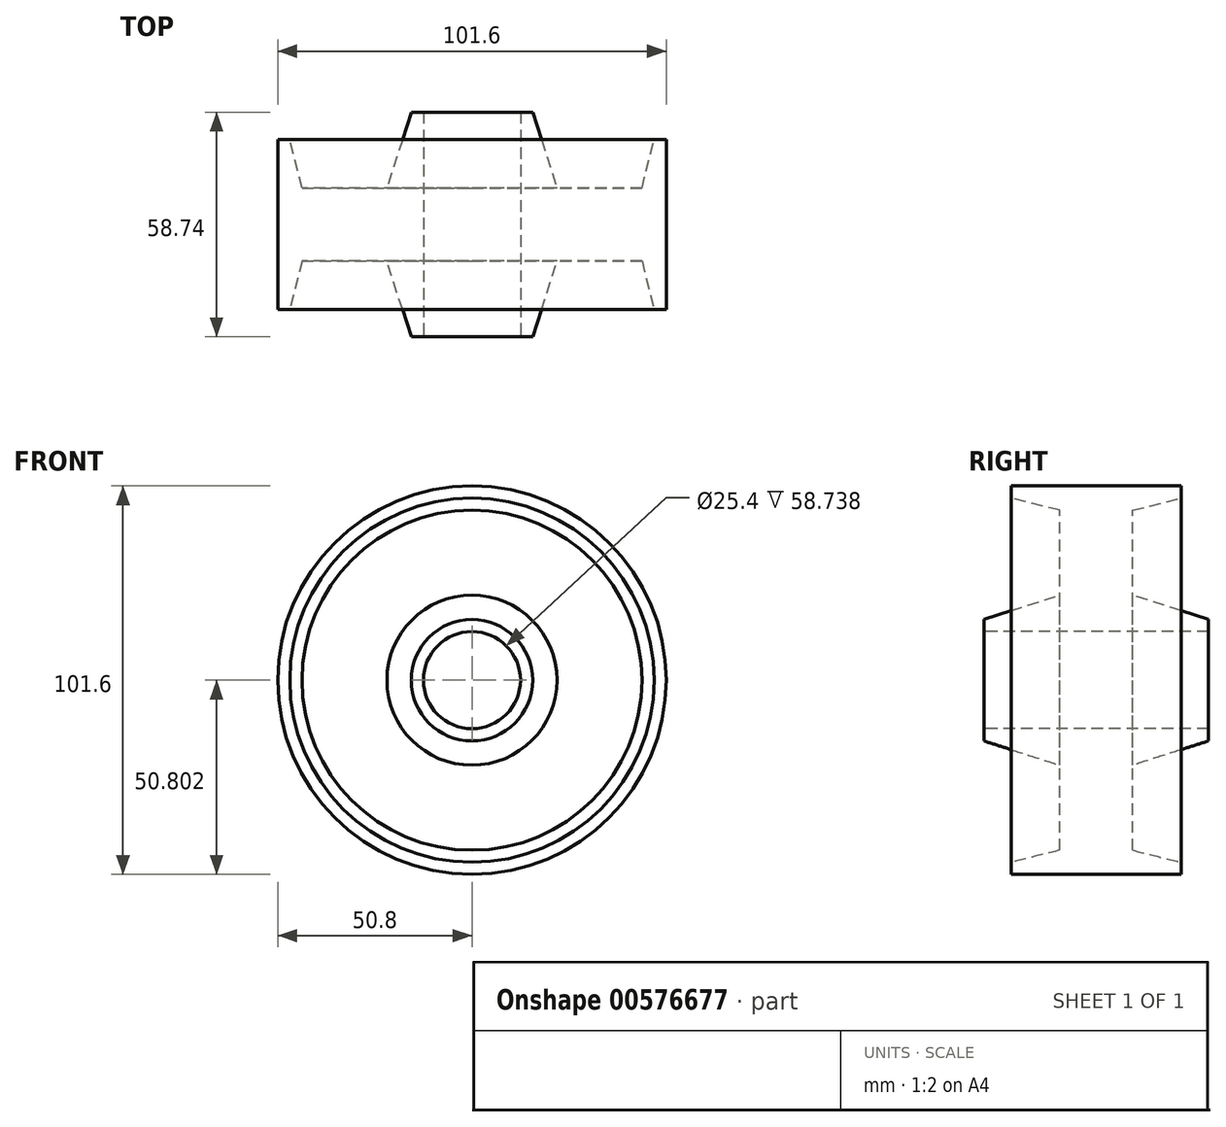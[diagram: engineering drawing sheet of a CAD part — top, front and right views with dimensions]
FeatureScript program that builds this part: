
annotation { "Feature Type Name" : "Feature", "Feature Type Description" : "" }
export const myFeature = defineFeature(function(context is Context, id is Id, definition is map)
    precondition{}
    {
        {
            var Q0;
            Q0=qCreatedBy(makeId("Right.planeOp"),FACE);
            var sketch = newSketch(context, id + "F0", { "sketchPlane" : qUnion([Q0])});
            skLineSegment(sketch, "E0", {"start": v(-48.97, 0) * mm, "end": v(61.54, 0) * mm});
            skLineSegment(sketch, "E1", {"start": v(-46.8, 36.4) * mm, "end": v(11.94, 36.4) * mm});
            skLineSegment(sketch, "E2", {"start": v(11.94, 36.4) * mm, "end": v(11.94, 39.58) * mm});
            skLineSegment(sketch, "E3", {"start": v(-46.8, 36.4) * mm, "end": v(-46.8, 39.58) * mm});
            skLineSegment(sketch, "E4", {"start": v(-17.43, 74.5) * mm, "end": v(4.8, 74.5) * mm});
            skLineSegment(sketch, "E5", {"start": v(-17.43, 74.5) * mm, "end": v(-39.66, 74.5) * mm});
            skLineSegment(sketch, "E6.0", {"start": v(-7.9, 36.4) * mm, "end": v(-7.9, 74.5) * mm});
            skLineSegment(sketch, "E7.0", {"start": v(-26.96, 36.4) * mm, "end": v(-26.96, 74.5) * mm});
            skLineSegment(sketch, "E8", {"start": v(-39.66, 74.5) * mm, "end": v(-39.66, 71.33) * mm});
            skLineSegment(sketch, "E9", {"start": v(4.8, 74.5) * mm, "end": v(4.8, 71.33) * mm});
            skLineSegment(sketch, "E10", {"start": v(-17.43, 23.7) * mm, "end": v(26.53, 23.7) * mm});
            skLineSegment(sketch, "E11", {"start": v(-7.9, 45.93) * mm, "end": v(11.94, 39.58) * mm});
            skLineSegment(sketch, "E12", {"start": v(-26.96, 45.93) * mm, "end": v(-46.8, 39.58) * mm});
            skLineSegment(sketch, "E13", {"start": v(-7.9, 68.15) * mm, "end": v(4.8, 71.33) * mm});
            skLineSegment(sketch, "E14", {"start": v(-26.96, 68.15) * mm, "end": v(-39.66, 71.33) * mm});
            skSolve(sketch);
        }
        {
            var Q0;
            Q0 = qSketchRegion(id + "F0", true);
            var Q1;
            Q1=sQuery(id+"F0.wireOp",EDGE,"E10");
            revolve(context, id + "F1", {"entities" : qUnion([Q0]), "axis" : qUnion([Q1]), "revolveType" : RevolveType.FULL});
        }
    });
